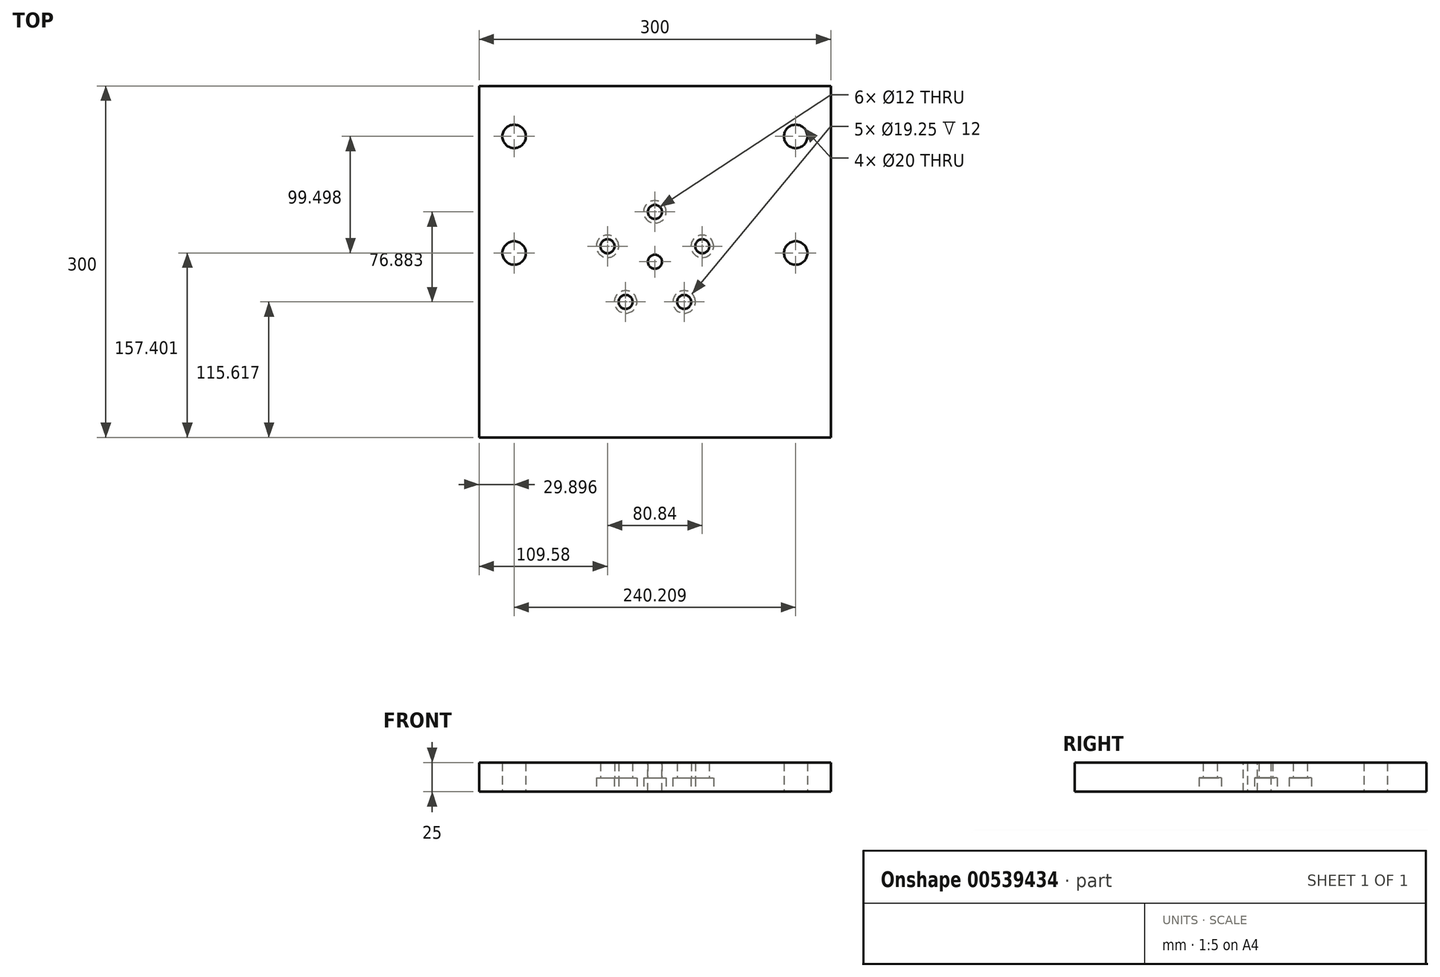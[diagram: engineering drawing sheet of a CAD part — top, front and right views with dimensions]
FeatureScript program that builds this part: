
annotation { "Feature Type Name" : "Feature", "Feature Type Description" : "" }
export const myFeature = defineFeature(function(context is Context, id is Id, definition is map)
    precondition{}
    {
        {
            var Q0;
            Q0=qCreatedBy(makeId("Top.planeOp"),FACE);
            var sketch = newSketch(context, id + "F0", { "sketchPlane" : qUnion([Q0])});
            skLineSegment(sketch, "E0.bottom", {"start": v(-150, 150) * mm, "end": v(150, 150) * mm});
            skLineSegment(sketch, "E0.top", {"start": v(-150, -150) * mm, "end": v(150, -150) * mm});
            skLineSegment(sketch, "E0.left", {"start": v(-150, 150) * mm, "end": v(-150, -150) * mm});
            skLineSegment(sketch, "E0.right", {"start": v(150, 150) * mm, "end": v(150, -150) * mm});
            skPoint(sketch, "E0.middle", {"position": v(0, 0) * mm});
            skSolve(sketch);
        }
        {
            var Q0;
            Q0 = qSketchRegion(id + "F0", true);
            extrude(context, id + "F1", {"entities" : qUnion([Q0]), "depth" : 25 * mm, "offsetDistance" : 25 * mm});
        }
        {
            var Q0;
            Q0=makeQuery(id+"F1.opExtrude","CAP_FACE",FACE,{"disambiguationData":[OSD([sQuery(id+"F0.wireOp",EDGE,"E0.bottom"),sQuery(id+"F0.wireOp",EDGE,"E0.top"),sQuery(id+"F0.wireOp",EDGE,"E0.left"),sQuery(id+"F0.wireOp",EDGE,"E0.right")])],"isStart":false});
            var sketch = newSketch(context, id + "F2", { "sketchPlane" : qUnion([Q0])});
            skLineSegment(sketch, "E1.bottom", {"start": v(-65, 65) * mm, "end": v(65, 65) * mm});
            skLineSegment(sketch, "E1.top", {"start": v(-65, -65) * mm, "end": v(65, -65) * mm});
            skLineSegment(sketch, "E1.left", {"start": v(-65, 65) * mm, "end": v(-65, -65) * mm});
            skLineSegment(sketch, "E1.right", {"start": v(65, 65) * mm, "end": v(65, -65) * mm});
            skPoint(sketch, "E2", {"position": v(0, 0) * mm});
            skSolve(sketch);
        }
        {
            var Q0;
            Q0=makeQuery(id+"F1.opExtrude","CAP_FACE",FACE,{"disambiguationData":[OSD([sQuery(id+"F0.wireOp",EDGE,"E0.bottom"),sQuery(id+"F0.wireOp",EDGE,"E0.top"),sQuery(id+"F0.wireOp",EDGE,"E0.left"),sQuery(id+"F0.wireOp",EDGE,"E0.right")])],"isStart":true});
            var sketch = newSketch(context, id + "F3", { "sketchPlane" : qUnion([Q0])});
            skCircle(sketch, "E3", {"center": v(0, 0) * mm, "radius": 42.5 * mm});
            skPoint(sketch, "E4", {"position": v(0, -42.5) * mm});
            skPoint(sketch, "E5.1.0", {"position": v(40.42, -13.13) * mm});
            skPoint(sketch, "E5.2.0", {"position": v(24.98, 34.38) * mm});
            skPoint(sketch, "E5.3.0", {"position": v(-24.98, 34.38) * mm});
            skPoint(sketch, "E5.4.0", {"position": v(-40.42, -13.13) * mm});
            skCircle(sketch, "E6", {"center": v(0, 0) * mm, "radius": 57.15 * mm});
            skPoint(sketch, "E7", {"position": v(0, -57.15) * mm});
            skCircle(sketch, "E8", {"center": v(0, -57.15) * mm, "radius": 130 * mm});
            skPoint(sketch, "E9", {"position": v(0, -187.15) * mm});
            skPoint(sketch, "E10.1.0", {"position": v(49.75, -177.25) * mm});
            skPoint(sketch, "E10.2.0", {"position": v(91.92, -149.07) * mm});
            skPoint(sketch, "E10.3.0", {"position": v(120.1, -106.9) * mm});
            skPoint(sketch, "E10.4.0", {"position": v(130, -57.15) * mm});
            skPoint(sketch, "E10.5.0", {"position": v(120.1, -7.4) * mm});
            skPoint(sketch, "E10.6.0", {"position": v(91.92, 34.77) * mm});
            skPoint(sketch, "E10.7.0", {"position": v(49.75, 62.95) * mm});
            skPoint(sketch, "E10.8.0", {"position": v(0, 72.85) * mm});
            skPoint(sketch, "E10.9.0", {"position": v(-49.75, 62.95) * mm});
            skPoint(sketch, "E10.10.0", {"position": v(-91.92, 34.77) * mm});
            skPoint(sketch, "E10.11.0", {"position": v(-120.1, -7.4) * mm});
            skPoint(sketch, "E10.12.0", {"position": v(-130, -57.15) * mm});
            skPoint(sketch, "E10.13.0", {"position": v(-120.1, -106.9) * mm});
            skPoint(sketch, "E10.14.0", {"position": v(-91.92, -149.07) * mm});
            skPoint(sketch, "E10.15.0", {"position": v(-49.75, -177.25) * mm});
            skSolve(sketch);
        }
        {
            var Q0;
            Q0=sQuery(id+"F3.wireOp",VERTEX,"E4");
            var Q1;
            Q1=sQuery(id+"F3.wireOp",VERTEX,"E5.4.0");
            var Q2;
            Q2=sQuery(id+"F3.wireOp",VERTEX,"E5.3.0");
            var Q3;
            Q3=sQuery(id+"F3.wireOp",VERTEX,"E5.2.0");
            var Q4;
            Q4=sQuery(id+"F3.wireOp",VERTEX,"E5.1.0");
            var Q5;
            Q5=makeQuery(id+"F1.opExtrude","SWEPT_BODY",BODY,{"disambiguationData":[OSD([sQuery(id+"F0.wireOp",EDGE,"E0.bottom"),sQuery(id+"F0.wireOp",EDGE,"E0.top"),sQuery(id+"F0.wireOp",EDGE,"E0.left"),sQuery(id+"F0.wireOp",EDGE,"E0.right")])]});
            hole(context, id + "F4", {"style" : HoleStyle.C_BORE, "endStyle" : HoleEndStyle.BLIND, "standardTappedOrClearance" : lookupTablePath({ "standard" : "ISO", "size" : "12", "type" : "Drilled" }), "standardBlindInLast" : lookupTablePath({ "standard" : "ISO", "size" : "12", "type" : "Drilled" }), "holeDiameter" : 12 * mm, "cBoreDiameter" : 19.25 * mm, "cBoreDepth" : 12 * mm, "majorDiameter" : 12 * mm, "holeDepth" : 35.25 * mm, "tappedDepth" : 30 * mm, "tapClearance" : 3, "locations" : qUnion([Q0, Q1, Q2, Q3, Q4]), "scope" : qUnion([Q5])});
        }
        {
            var Q0;
            Q0=sQuery(id+"F2.wireOp",VERTEX,"E2");
            var Q1;
            Q1=makeQuery(id+"F1.opExtrude","SWEPT_BODY",BODY,{"disambiguationData":[OSD([sQuery(id+"F0.wireOp",EDGE,"E0.bottom"),sQuery(id+"F0.wireOp",EDGE,"E0.top"),sQuery(id+"F0.wireOp",EDGE,"E0.left"),sQuery(id+"F0.wireOp",EDGE,"E0.right")])]});
            hole(context, id + "F5", {"style" : HoleStyle.SIMPLE, "endStyle" : HoleEndStyle.THROUGH, "standardTappedOrClearance" : lookupTablePath({ "standard" : "ISO", "size" : "12", "type" : "Drilled" }), "standardBlindInLast" : lookupTablePath({ "standard" : "ISO", "size" : "12", "type" : "Drilled" }), "holeDiameter" : 12 * mm, "majorDiameter" : 5 * mm, "tappedDepth" : 20 * mm, "tapClearance" : 3, "locations" : qUnion([Q0]), "scope" : qUnion([Q1])});
        }
        {
            var Q0;
            Q0=sQuery(id+"F3.wireOp",VERTEX,"E10.13.0");
            var Q1;
            Q1=sQuery(id+"F3.wireOp",VERTEX,"E10.11.0");
            var Q2;
            Q2=sQuery(id+"F3.wireOp",VERTEX,"E10.5.0");
            var Q3;
            Q3=sQuery(id+"F3.wireOp",VERTEX,"E10.3.0");
            var Q4;
            Q4=makeQuery(id+"F1.opExtrude","SWEPT_BODY",BODY,{"disambiguationData":[OSD([sQuery(id+"F0.wireOp",EDGE,"E0.bottom"),sQuery(id+"F0.wireOp",EDGE,"E0.top"),sQuery(id+"F0.wireOp",EDGE,"E0.left"),sQuery(id+"F0.wireOp",EDGE,"E0.right")])]});
            hole(context, id + "F6", {"style" : HoleStyle.SIMPLE, "endStyle" : HoleEndStyle.BLIND, "standardTappedOrClearance" : lookupTablePath({ "standard" : "ISO", "size" : "20", "type" : "Drilled" }), "standardBlindInLast" : lookupTablePath({ "standard" : "ISO", "size" : "20", "type" : "Drilled" }), "holeDiameter" : 20 * mm, "majorDiameter" : 5 * mm, "holeDepth" : 25 * mm, "tappedDepth" : 30 * mm, "tapClearance" : 3, "locations" : qUnion([Q0, Q1, Q2, Q3]), "scope" : qUnion([Q4])});
        }
    });
